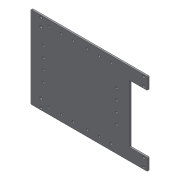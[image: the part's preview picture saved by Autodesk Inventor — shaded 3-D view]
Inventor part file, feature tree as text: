
AUTODESK INVENTOR PART (.ipt)
format: ipt  version: 2018 (Build 220112000, 112)  size: 197,120 bytes
history: native  units: mm
features: sketch x8, extrude x5, hole x3, mirror x3, plane x2, projected_geometry x2, fillet x1
ambient origin geometry x8: Origin, YZ Plane, XZ Plane, XY Plane, X Axis, Y Axis, Z Axis, Center Point
bodies: Solid1 (feature_tree)
feature tree (24):
  extrude  "Extrusion1"  Depth=172.0mm
  hole  "Hole1"  [1 undecoded]
  mirror  "Mirror1"
  extrude  "Extrusion2"  Depth=25.4mm TaperAngle=0.0deg
  extrude  "Extrusion3"  Depth=21.4376mm
  hole  "Hole2"  [1 undecoded]
  plane  "Work Plane2"
  mirror  "Mirror3"
  mirror  "Mirror4"
  hole  "Hole3"  [1 undecoded]
  extrude  "Extrusion4"  Depth=1.6mm TaperAngle=0.0deg
  fillet  "Fillet2"  Radius=25.4mm
  extrude  "Extrusion5"  Depth=121.2mm
  sketch  "Sketch1"  dims[d0=156.0mm d1=172.0mm]
  sketch  "Sketch2"  dims[d2=3.175mm d3=0.0mm d4=50.8mm]
  plane  "Work Plane1"
  sketch  "Sketch3"  dims[d5=12.7mm]
  projected_geometry  "Projected Loop1"
  sketch  "Sketch4"  dims[d7=4.5mm d8=6.0mm d9=9.4mm d10=2.0mm d11=90.0deg d12=8.0mm d13=20.594885mm d14=25.4mm d15=0.0mm]
  sketch  "Sketch5"  dims[d16=17.4625mm d17=21.4376mm]
  sketch  "Sketch6"  dims[d18=5.3mm d19=0.599mm d20=10.4mm d21=2.0mm d22=90.0deg d23=8.0mm d24=20.594885mm d26=66.0mm]
  projected_geometry  "Projected Loop2"
  sketch  "Sketch7"  dims[d28=4.5mm d29=6.0mm d30=9.4mm d31=2.0mm d32=90.0deg d33=8.0mm d34=20.594885mm d35=27.0mm]
  sketch  "Sketch8"  dims[d36=22.0mm d37=63.5mm d38=0.0mm d39=25.4mm d40=121.2mm d41=38.1mm d42=63.5mm d43=0.0mm d44=2.0mm d45=38.1mm d46=56.5mm d47=45.5mm d48=1.6mm d49=0.0mm]
note: 3 required parameter values undecoded (feature->parameter linkage not recoverable at this tier; creation-order binding heuristic only, values carry confidence <= 0.55)
